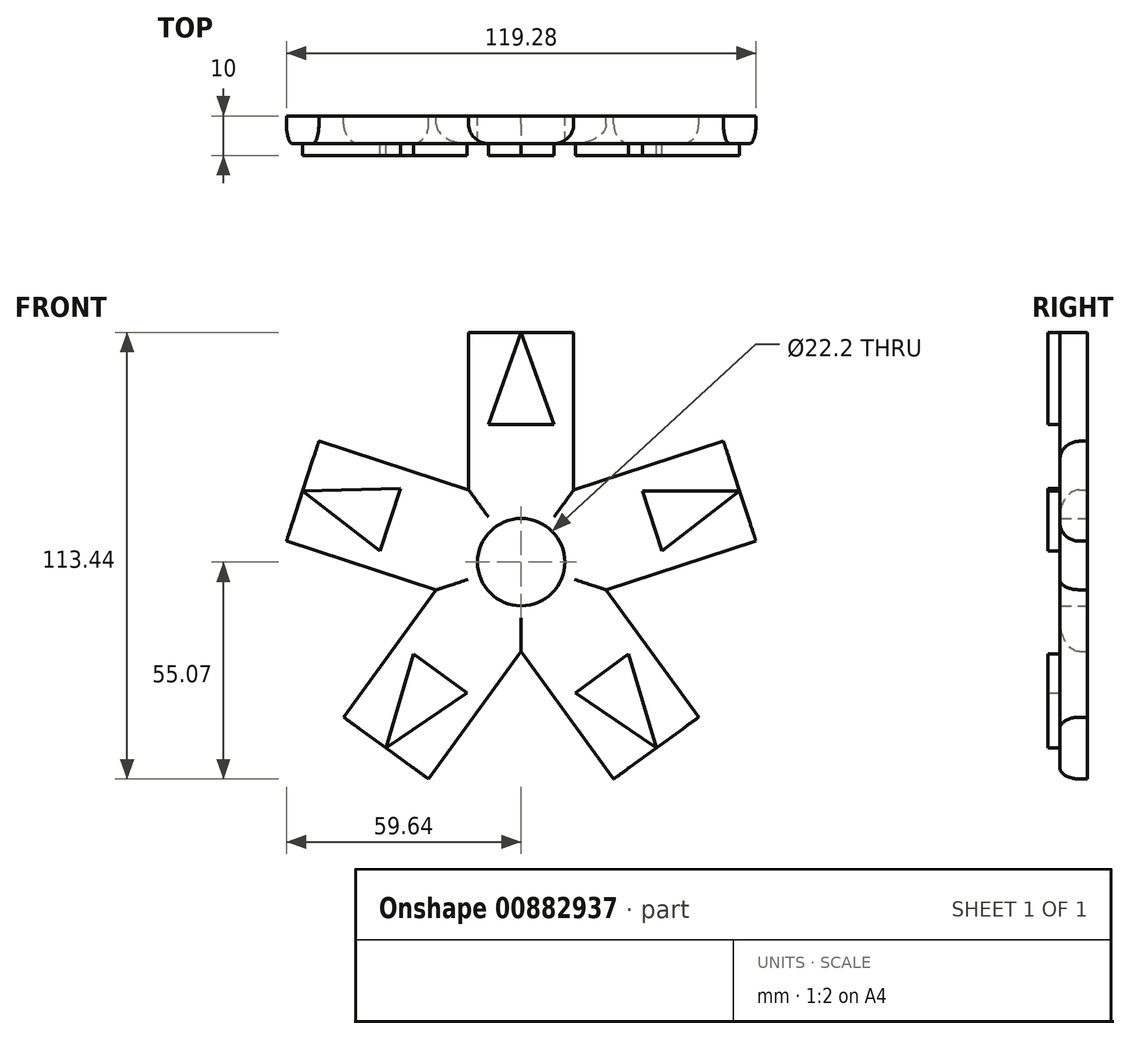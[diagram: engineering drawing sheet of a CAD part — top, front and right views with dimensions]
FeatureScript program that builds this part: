
annotation { "Feature Type Name" : "Feature", "Feature Type Description" : "" }
export const myFeature = defineFeature(function(context is Context, id is Id, definition is map)
    precondition{}
    {
        {
            var Q0;
            Q0=qCreatedBy(makeId("Front.planeOp"),FACE);
            var sketch = newSketch(context, id + "F0", { "sketchPlane" : qUnion([Q0])});
            skCircle(sketch, "E0.cCircle", {"center": v(0, 0) * mm, "radius": 22.7 * mm, "construction": true});
            skLineSegment(sketch, "E0.0", {"start": v(0, -22.7) * mm, "end": v(-21.6, -7.02) * mm});
            skLineSegment(sketch, "E0.1", {"start": v(-21.6, -7.02) * mm, "end": v(-13.35, 18.37) * mm});
            skLineSegment(sketch, "E0.2", {"start": v(-13.35, 18.37) * mm, "end": v(13.35, 18.37) * mm});
            skLineSegment(sketch, "E0.3", {"start": v(13.35, 18.37) * mm, "end": v(21.6, -7.02) * mm});
            skLineSegment(sketch, "E0.4", {"start": v(21.6, -7.02) * mm, "end": v(0, -22.7) * mm});
            skLineSegment(sketch, "E1", {"start": v(-13.35, 18.37) * mm, "end": v(-13.35, 58.37) * mm});
            skLineSegment(sketch, "E2", {"start": v(13.35, 18.37) * mm, "end": v(13.35, 58.37) * mm});
            skLineSegment(sketch, "E3", {"start": v(13.35, 58.37) * mm, "end": v(-13.35, 58.37) * mm});
            skLineSegment(sketch, "E4", {"start": v(-21.6, -7.02) * mm, "end": v(-59.64, 5.34) * mm});
            skLineSegment(sketch, "E5", {"start": v(-13.35, 18.37) * mm, "end": v(-51.39, 30.73) * mm});
            skLineSegment(sketch, "E6", {"start": v(-51.39, 30.73) * mm, "end": v(-59.64, 5.34) * mm});
            skLineSegment(sketch, "E7", {"start": v(13.35, 18.37) * mm, "end": v(51.39, 30.73) * mm});
            skLineSegment(sketch, "E8", {"start": v(51.39, 30.73) * mm, "end": v(59.64, 5.34) * mm});
            skLineSegment(sketch, "E9", {"start": v(59.64, 5.34) * mm, "end": v(21.6, -7.02) * mm});
            skLineSegment(sketch, "E10", {"start": v(-21.6, -7.02) * mm, "end": v(-45.1, -39.38) * mm});
            skLineSegment(sketch, "E11", {"start": v(-45.1, -39.38) * mm, "end": v(-23.51, -55.07) * mm});
            skLineSegment(sketch, "E12", {"start": v(-23.51, -55.07) * mm, "end": v(0, -22.7) * mm});
            skLineSegment(sketch, "E13", {"start": v(0, -22.7) * mm, "end": v(23.51, -55.07) * mm});
            skLineSegment(sketch, "E14", {"start": v(23.51, -55.07) * mm, "end": v(45.1, -39.38) * mm});
            skLineSegment(sketch, "E15", {"start": v(45.1, -39.38) * mm, "end": v(21.6, -7.02) * mm});
            skSolve(sketch);
        }
        {
            var Q0;
            Q0 = qSketchRegion(id + "F0", true);
            extrude(context, id + "F1", {"entities" : qUnion([Q0]), "depth" : 7 * mm, "offsetDistance" : 25 * mm});
        }
        {
            var Q0;
            Q0=makeQuery(id+"F1.opExtrude","CAP_EDGE",EDGE,{"disambiguationData":[OSD([sQuery(id+"F0.wireOp",EDGE,"E4")])],"isStart":false});
            var Q1;
            Q1=makeQuery(id+"F1.opExtrude","CAP_EDGE",EDGE,{"disambiguationData":[OSD([sQuery(id+"F0.wireOp",EDGE,"E5")])],"isStart":false});
            var Q2;
            Q2=makeQuery(id+"F1.opExtrude","CAP_EDGE",EDGE,{"disambiguationData":[OSD([sQuery(id+"F0.wireOp",EDGE,"E12")])],"isStart":false});
            var Q3;
            Q3=makeQuery(id+"F1.opExtrude","CAP_EDGE",EDGE,{"disambiguationData":[OSD([sQuery(id+"F0.wireOp",EDGE,"E9")])],"isStart":false});
            var Q4;
            Q4=makeQuery(id+"F1.opExtrude","CAP_EDGE",EDGE,{"disambiguationData":[OSD([sQuery(id+"F0.wireOp",EDGE,"E10")])],"isStart":false});
            var Q5;
            Q5=makeQuery(id+"F1.opExtrude","CAP_EDGE",EDGE,{"disambiguationData":[OSD([sQuery(id+"F0.wireOp",EDGE,"E15")])],"isStart":false});
            var Q6;
            Q6=makeQuery(id+"F1.opExtrude","CAP_EDGE",EDGE,{"disambiguationData":[OSD([sQuery(id+"F0.wireOp",EDGE,"E13")])],"isStart":false});
            var Q7;
            Q7=makeQuery(id+"F1.opExtrude","CAP_EDGE",EDGE,{"disambiguationData":[OSD([sQuery(id+"F0.wireOp",EDGE,"E7")])],"isStart":false});
            var Q8;
            Q8=makeQuery(id+"F1.opExtrude","CAP_EDGE",EDGE,{"disambiguationData":[OSD([sQuery(id+"F0.wireOp",EDGE,"E2")])],"isStart":false});
            var Q9;
            Q9=makeQuery(id+"F1.opExtrude","CAP_EDGE",EDGE,{"disambiguationData":[OSD([sQuery(id+"F0.wireOp",EDGE,"E1")])],"isStart":false});
            fillet(context, id + "F2", {"entities" : qUnion([Q0, Q1, Q2, Q3, Q4, Q5, Q6, Q7, Q8, Q9]), "radius" : 5 * mm, "tangentPropagation" : true, "allowEdgeOverflow" : false});
        }
        {
            var Q0;
            Q0=makeQuery(id+"F1.opExtrude","CAP_FACE",FACE,{"disambiguationData":[OSD([sQuery(id+"F0.wireOp",EDGE,"E1"),sQuery(id+"F0.wireOp",EDGE,"E2"),sQuery(id+"F0.wireOp",EDGE,"E3"),sQuery(id+"F0.wireOp",EDGE,"E4"),sQuery(id+"F0.wireOp",EDGE,"E5"),sQuery(id+"F0.wireOp",EDGE,"E6"),sQuery(id+"F0.wireOp",EDGE,"E7"),sQuery(id+"F0.wireOp",EDGE,"E8"),sQuery(id+"F0.wireOp",EDGE,"E9"),sQuery(id+"F0.wireOp",EDGE,"E10"),sQuery(id+"F0.wireOp",EDGE,"E11"),sQuery(id+"F0.wireOp",EDGE,"E12"),sQuery(id+"F0.wireOp",EDGE,"E13"),sQuery(id+"F0.wireOp",EDGE,"E14"),sQuery(id+"F0.wireOp",EDGE,"E15")])],"isStart":false});
            var sketch = newSketch(context, id + "F3", { "sketchPlane" : qUnion([Q0])});
            skLineSegment(sketch, "E16", {"start": v(-35.8, 2.86) * mm, "end": v(-30.64, 18.73) * mm});
            skLineSegment(sketch, "E17", {"start": v(-30.64, 18.73) * mm, "end": v(-55.51, 18.04) * mm});
            skLineSegment(sketch, "E18", {"start": v(-55.51, 18.04) * mm, "end": v(-35.8, 2.86) * mm});
            skLineSegment(sketch, "E19", {"start": v(-27.28, -23.35) * mm, "end": v(-13.78, -33.17) * mm});
            skLineSegment(sketch, "E20", {"start": v(-13.78, -33.17) * mm, "end": v(-34.3, -47.22) * mm});
            skLineSegment(sketch, "E21", {"start": v(-34.3, -47.22) * mm, "end": v(-27.28, -23.35) * mm});
            skLineSegment(sketch, "E22", {"start": v(13.78, -33.17) * mm, "end": v(27.28, -23.35) * mm});
            skLineSegment(sketch, "E23", {"start": v(27.28, -23.35) * mm, "end": v(34.3, -47.22) * mm});
            skLineSegment(sketch, "E24", {"start": v(34.3, -47.22) * mm, "end": v(13.78, -33.17) * mm});
            skLineSegment(sketch, "E25", {"start": v(30.64, 18.04) * mm, "end": v(55.51, 18.04) * mm});
            skPoint(sketch, "E25.startSnap0", {"position": v(30.64, 18.73) * mm});
            skLineSegment(sketch, "E26", {"start": v(55.51, 18.04) * mm, "end": v(35.8, 2.86) * mm});
            skLineSegment(sketch, "E27", {"start": v(35.8, 2.86) * mm, "end": v(30.64, 18.73) * mm});
            skLineSegment(sketch, "E28", {"start": v(8.35, 34.93) * mm, "end": v(-8.35, 34.93) * mm});
            skLineSegment(sketch, "E29", {"start": v(-8.35, 34.93) * mm, "end": v(0, 58.37) * mm});
            skLineSegment(sketch, "E30", {"start": v(0, 58.37) * mm, "end": v(8.35, 34.93) * mm});
            skSolve(sketch);
        }
        {
            var Q0;
            Q0=makeQuery(id+"F3.imprint","IMPRINT",FACE,{"disambiguationData":[TD([[makeQuery(id+"F3.imprint","IMPRINT",EDGE,{"derivedFrom":sQuery(id+"F3.wireOp",EDGE,"E16")}),1.0]])]});
            var Q1;
            Q1=makeQuery(id+"F3.imprint","IMPRINT",FACE,{"disambiguationData":[TD([[makeQuery(id+"F3.imprint","IMPRINT",EDGE,{"derivedFrom":sQuery(id+"F3.wireOp",EDGE,"E28")}),-1.0]])]});
            var Q2;
            {var subQ0=sQuery(id+"F3.wireOp",EDGE,"E26");Q2=makeQuery(id+"F3.imprint","IMPRINT",FACE,{"disambiguationData":[TD([[makeQuery(id+"F3.imprint","IMPRINT",EDGE,{"derivedFrom":subQ0}),-1.0]])]});}
            var Q3;
            Q3=makeQuery(id+"F3.imprint","IMPRINT",FACE,{"disambiguationData":[TD([[makeQuery(id+"F3.imprint","IMPRINT",EDGE,{"derivedFrom":sQuery(id+"F3.wireOp",EDGE,"E22")}),-1.0]])]});
            var Q4;
            Q4=makeQuery(id+"F3.imprint","IMPRINT",FACE,{"disambiguationData":[TD([[makeQuery(id+"F3.imprint","IMPRINT",EDGE,{"derivedFrom":sQuery(id+"F3.wireOp",EDGE,"E19")}),-1.0]])]});
            extrude(context, id + "F4", {"entities" : qUnion([Q0, Q1, Q2, Q3, Q4]), "operationType" : NewBodyOperationType.ADD, "depth" : 3 * mm, "offsetDistance" : 25 * mm});
        }
        {
            var Q0;
            Q0=qCreatedBy(makeId("Front.planeOp"),FACE);
            var sketch = newSketch(context, id + "F5", { "sketchPlane" : qUnion([Q0])});
            skPoint(sketch, "E31", {"position": v(0, 0) * mm});
            skSolve(sketch);
        }
        {
            var Q0;
            Q0=sQuery(id+"F5.wireOp",VERTEX,"E31");
            var Q1;
            Q1=makeQuery(id+"F1.opExtrude","SWEPT_BODY",BODY,{"disambiguationData":[OSD([sQuery(id+"F0.wireOp",EDGE,"E1"),sQuery(id+"F0.wireOp",EDGE,"E2"),sQuery(id+"F0.wireOp",EDGE,"E3"),sQuery(id+"F0.wireOp",EDGE,"E4"),sQuery(id+"F0.wireOp",EDGE,"E5"),sQuery(id+"F0.wireOp",EDGE,"E6"),sQuery(id+"F0.wireOp",EDGE,"E7"),sQuery(id+"F0.wireOp",EDGE,"E8"),sQuery(id+"F0.wireOp",EDGE,"E9"),sQuery(id+"F0.wireOp",EDGE,"E10"),sQuery(id+"F0.wireOp",EDGE,"E11"),sQuery(id+"F0.wireOp",EDGE,"E12"),sQuery(id+"F0.wireOp",EDGE,"E13"),sQuery(id+"F0.wireOp",EDGE,"E14"),sQuery(id+"F0.wireOp",EDGE,"E15")])]});
            hole(context, id + "F6", {"style" : HoleStyle.SIMPLE, "endStyle" : HoleEndStyle.BLIND, "oppositeDirection" : true, "holeDiameter" : 22.2 * mm, "majorDiameter" : 5 * mm, "holeDepth" : 20 * mm, "isTappedThrough" : true, "tappedDepth" : 12 * mm, "tapClearance" : 3, "locations" : qUnion([Q0]), "scope" : qUnion([Q1])});
        }
    });
